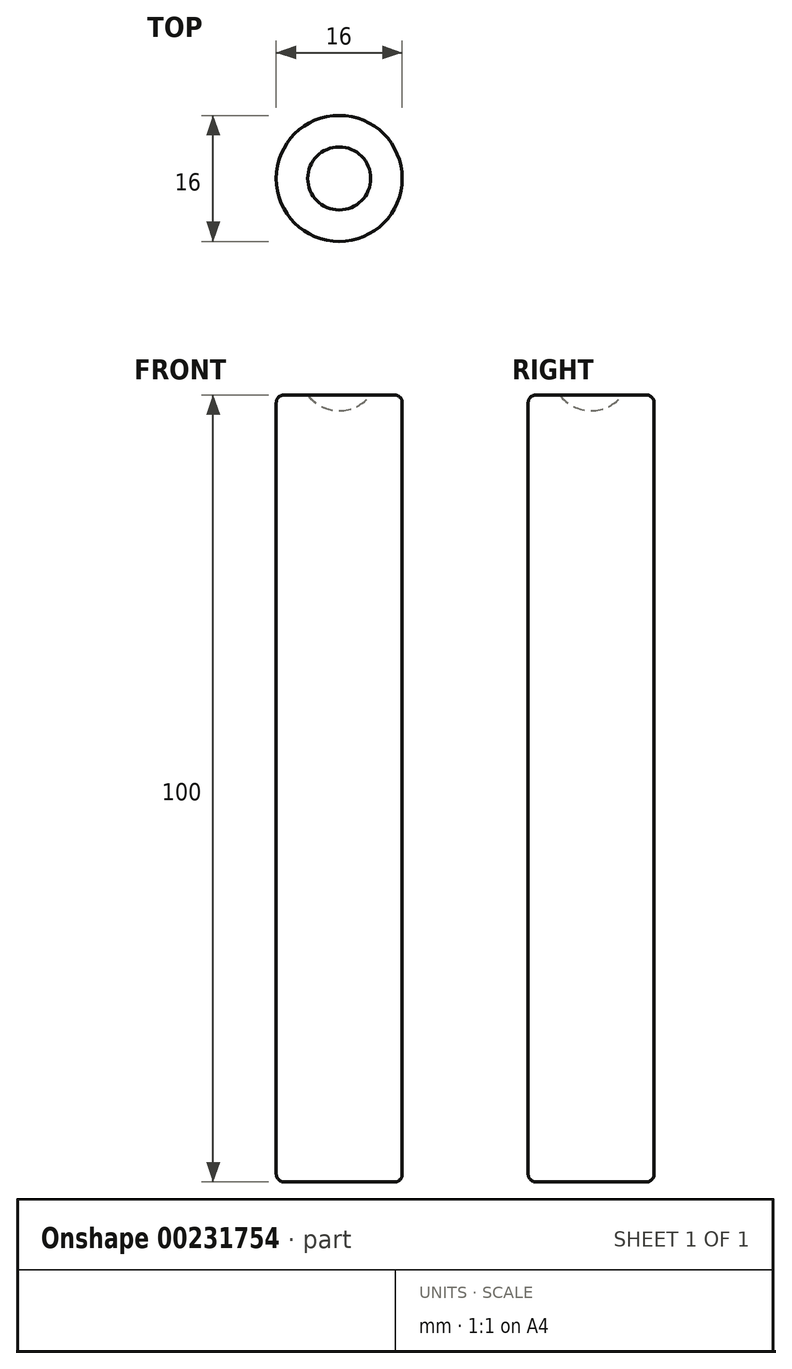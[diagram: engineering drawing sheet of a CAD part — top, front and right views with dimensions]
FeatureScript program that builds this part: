
annotation { "Feature Type Name" : "Feature", "Feature Type Description" : "" }
export const myFeature = defineFeature(function(context is Context, id is Id, definition is map)
    precondition{}
    {
        {
            var Q0;
            Q0=qCreatedBy(makeId("Top.planeOp"),FACE);
            var sketch = newSketch(context, id + "F0", { "sketchPlane" : qUnion([Q0])});
            skCircle(sketch, "E0", {"center": v(0, 0) * mm, "radius": 8 * mm});
            skSolve(sketch);
        }
        {
            var Q0;
            Q0 = qSketchRegion(id + "F0", true);
            extrude(context, id + "F1", {"entities" : qUnion([Q0]), "depth" : 50 * mm, "hasSecondDirection" : true, "secondDirectionOppositeDirection" : true, "secondDirectionDepth" : 50 * mm});
        }
        {
            var Q0;
            Q0=qCreatedBy(makeId("Front.planeOp"),FACE);
            var sketch = newSketch(context, id + "F2", { "sketchPlane" : qUnion([Q0])});
            skLineSegment(sketch, "E1", {"start": v(0, 0) * mm, "end": v(0, 53) * mm});
            skCircle(sketch, "E2", {"center": v(0, 53) * mm, "radius": 5 * mm});
            skLineSegment(sketch, "E3", {"start": v(0, 58) * mm, "end": v(0, 48) * mm});
            skSolve(sketch);
        }
        {
            var Q0;
            {var subQ0=sQuery(id+"F2.wireOp",EDGE,"E3");var subQ4=makeQuery(id+"F2.imprint","IMPRINT",VERTEX,{"derivedFrom":subQ0});Q0=makeQuery(id+"F2.imprint","IMPRINT",FACE,{"disambiguationData":[TD([[makeQuery(id+"F2.imprint","IMPRINT",EDGE,{"disambiguationData":[TD([[subQ4,1.0]])],"derivedFrom":subQ0}),1.0]])]});}
            var Q1;
            Q1=sQuery(id+"F2.wireOp",EDGE,"E3");
            revolve(context, id + "F3", {"operationType" : NewBodyOperationType.REMOVE, "entities" : qUnion([Q0]), "axis" : qUnion([Q1]), "revolveType" : RevolveType.FULL, "oppositeDirection" : true});
        }
        {
            var Q0;
            Q0=makeQuery(id+"F1.opExtrude","CAP_EDGE",EDGE,{"disambiguationData":[OSD([sQuery(id+"F0.wireOp",EDGE,"E0")])],"isStart":false});
            var Q1;
            Q1=makeQuery(id+"F1.opExtrude","CAP_EDGE",EDGE,{"disambiguationData":[OSD([sQuery(id+"F0.wireOp",EDGE,"E0")])],"isStart":true});
            fillet(context, id + "F4", {"entities" : qUnion([Q0, Q1]), "radius" : 1 * mm, "tangentPropagation" : true, "allowEdgeOverflow" : false});
        }
    });
